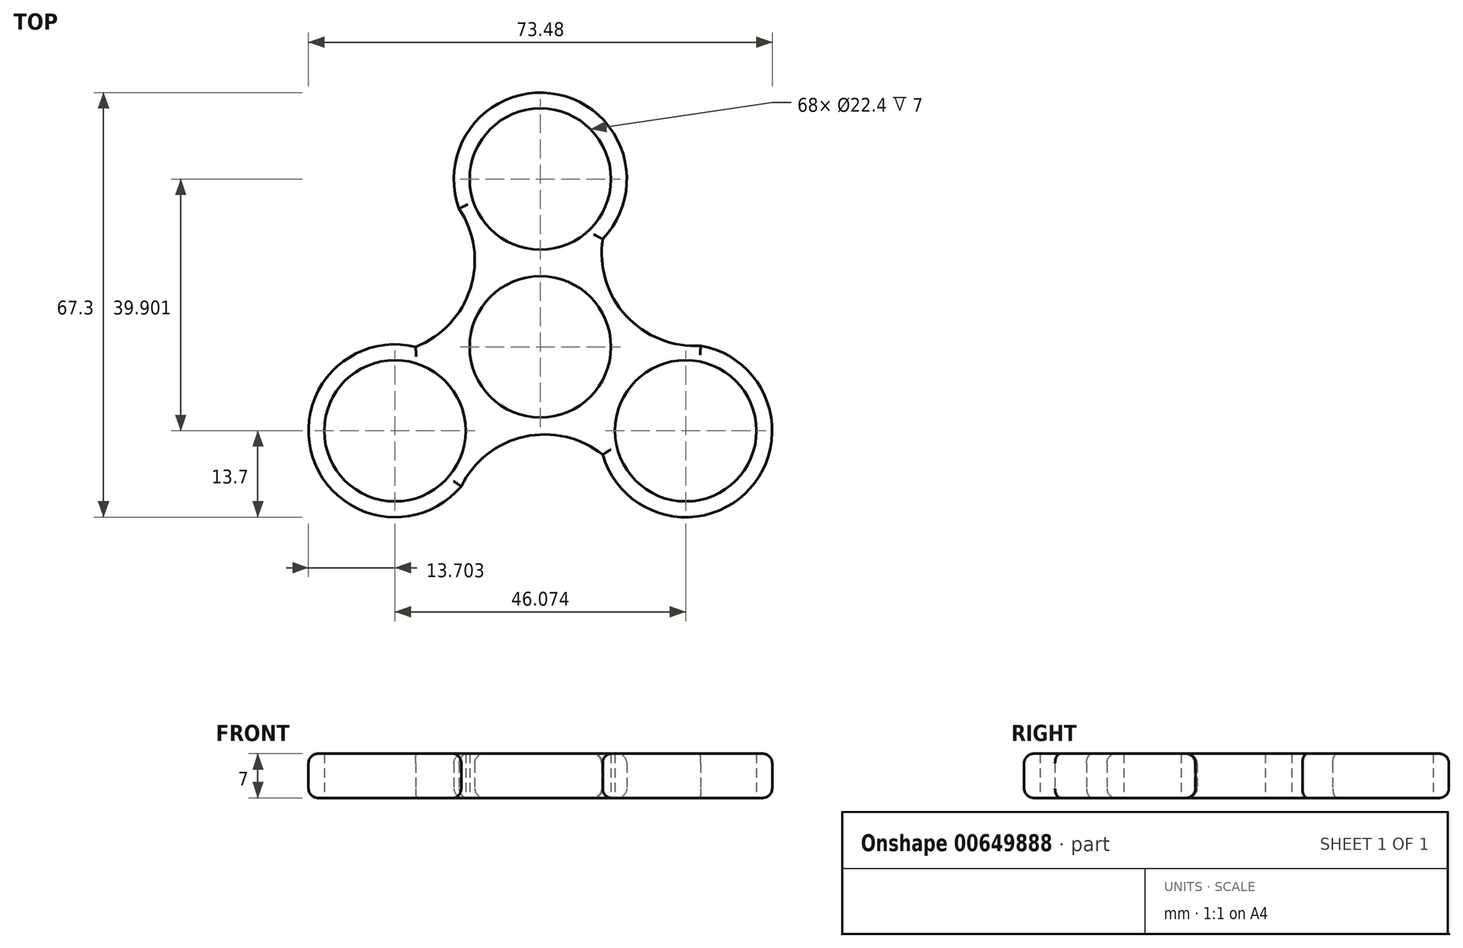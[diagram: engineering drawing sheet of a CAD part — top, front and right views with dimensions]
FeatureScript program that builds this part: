
annotation { "Feature Type Name" : "Feature", "Feature Type Description" : "" }
export const myFeature = defineFeature(function(context is Context, id is Id, definition is map)
    precondition{}
    {
        {
            var Q0;
            Q0=qCreatedBy(makeId("Top.planeOp"),FACE);
            var sketch = newSketch(context, id + "F0", { "sketchPlane" : qUnion([Q0])});
            skCircle(sketch, "E0", {"center": v(0, 0) * mm, "radius": 11.2 * mm});
            skCircle(sketch, "E1", {"center": v(0, 26.6) * mm, "radius": 11.2 * mm});
            skCircle(sketch, "E2.1.0", {"center": v(-23.04, -13.3) * mm, "radius": 11.2 * mm});
            skArc(sketch, "E2.1.1", {"start": v(-19.75, 0) * mm, "mid": v(-35.43, -19.13) * mm, "end": v(-10.7, -19.25) * mm});
            skCircle(sketch, "E2.2.0", {"center": v(23.04, -13.3) * mm, "radius": 11.2 * mm});
            skArc(sketch, "E2.2.1", {"start": v(9.88, -17.1) * mm, "mid": v(34.29, -21.12) * mm, "end": v(22.02, 0.36) * mm});
            skArc(sketch, "E3", {"start": v(-19.75, 0) * mm, "mid": v(-11.06, 9.3) * mm, "end": v(-12.87, 21.9) * mm});
            skArc(sketch, "E4.1.0", {"start": v(9.88, -17.1) * mm, "mid": v(-2.53, -14.23) * mm, "end": v(-12.54, -22.1) * mm});
            skArc(sketch, "E4.2.0", {"start": v(9.88, 17.1) * mm, "mid": v(13.6, 4.93) * mm, "end": v(25.4, 0.2) * mm});
            skArc(sketch, "E5.trimOffspring", {"start": v(9.88, 17.1) * mm, "mid": v(1.15, 40.25) * mm, "end": v(-11.32, 18.89) * mm});
            skSolve(sketch);
        }
        {
            var Q0;
            Q0=makeQuery(id+"F0.imprint","IMPRINT",FACE,{"disambiguationData":[TD([[makeQuery(id+"F0.imprint","IMPRINT",EDGE,{"derivedFrom":sQuery(id+"F0.wireOp",EDGE,"E0")}),-1.0]])]});
            extrude(context, id + "F1", {"entities" : qUnion([Q0]), "depth" : 7 * mm, "offsetDistance" : 25 * mm});
        }
        {
            var Q0;
            Q0=makeQuery(id+"F1.opExtrude","CAP_EDGE",EDGE,{"disambiguationData":[OSD([sQuery(id+"F0.wireOp",EDGE,"E5.trimOffspring")])],"isStart":false});
            var Q1;
            Q1=makeQuery(id+"F1.opExtrude","CAP_EDGE",EDGE,{"disambiguationData":[OSD([sQuery(id+"F0.wireOp",EDGE,"E4.2.0")])],"isStart":false});
            var Q2;
            Q2=makeQuery(id+"F1.opExtrude","CAP_EDGE",EDGE,{"disambiguationData":[OSD([sQuery(id+"F0.wireOp",EDGE,"E2.2.1")])],"isStart":false});
            var Q3;
            Q3=makeQuery(id+"F1.opExtrude","CAP_EDGE",EDGE,{"disambiguationData":[OSD([sQuery(id+"F0.wireOp",EDGE,"E4.1.0")])],"isStart":false});
            var Q4;
            Q4=makeQuery(id+"F1.opExtrude","CAP_EDGE",EDGE,{"disambiguationData":[OSD([sQuery(id+"F0.wireOp",EDGE,"E2.1.1")])],"isStart":false});
            var Q5;
            Q5=makeQuery(id+"F1.opExtrude","CAP_EDGE",EDGE,{"disambiguationData":[OSD([sQuery(id+"F0.wireOp",EDGE,"E3")])],"isStart":false});
            fillet(context, id + "F2", {"entities" : qUnion([Q0, Q1, Q2, Q3, Q4, Q5]), "radius" : 1.5 * mm, "tangentPropagation" : true, "allowEdgeOverflow" : false});
        }
        {
            var Q0;
            Q0=makeQuery(id+"F1.opExtrude","CAP_EDGE",EDGE,{"disambiguationData":[OSD([sQuery(id+"F0.wireOp",EDGE,"E3")])],"isStart":true});
            var Q1;
            Q1=makeQuery(id+"F1.opExtrude","CAP_EDGE",EDGE,{"disambiguationData":[OSD([sQuery(id+"F0.wireOp",EDGE,"E5.trimOffspring")])],"isStart":true});
            var Q2;
            Q2=makeQuery(id+"F1.opExtrude","CAP_EDGE",EDGE,{"disambiguationData":[OSD([sQuery(id+"F0.wireOp",EDGE,"E2.1.1")])],"isStart":true});
            var Q3;
            Q3=makeQuery(id+"F1.opExtrude","CAP_EDGE",EDGE,{"disambiguationData":[OSD([sQuery(id+"F0.wireOp",EDGE,"E2.2.1")])],"isStart":true});
            var Q4;
            Q4=makeQuery(id+"F1.opExtrude","CAP_EDGE",EDGE,{"disambiguationData":[OSD([sQuery(id+"F0.wireOp",EDGE,"E4.2.0")])],"isStart":true});
            var Q5;
            Q5=makeQuery(id+"F1.opExtrude","CAP_EDGE",EDGE,{"disambiguationData":[OSD([sQuery(id+"F0.wireOp",EDGE,"E4.1.0")])],"isStart":true});
            fillet(context, id + "F3", {"entities" : qUnion([Q0, Q1, Q2, Q3, Q4, Q5]), "radius" : 1.5 * mm, "tangentPropagation" : true, "allowEdgeOverflow" : false});
        }
    });
